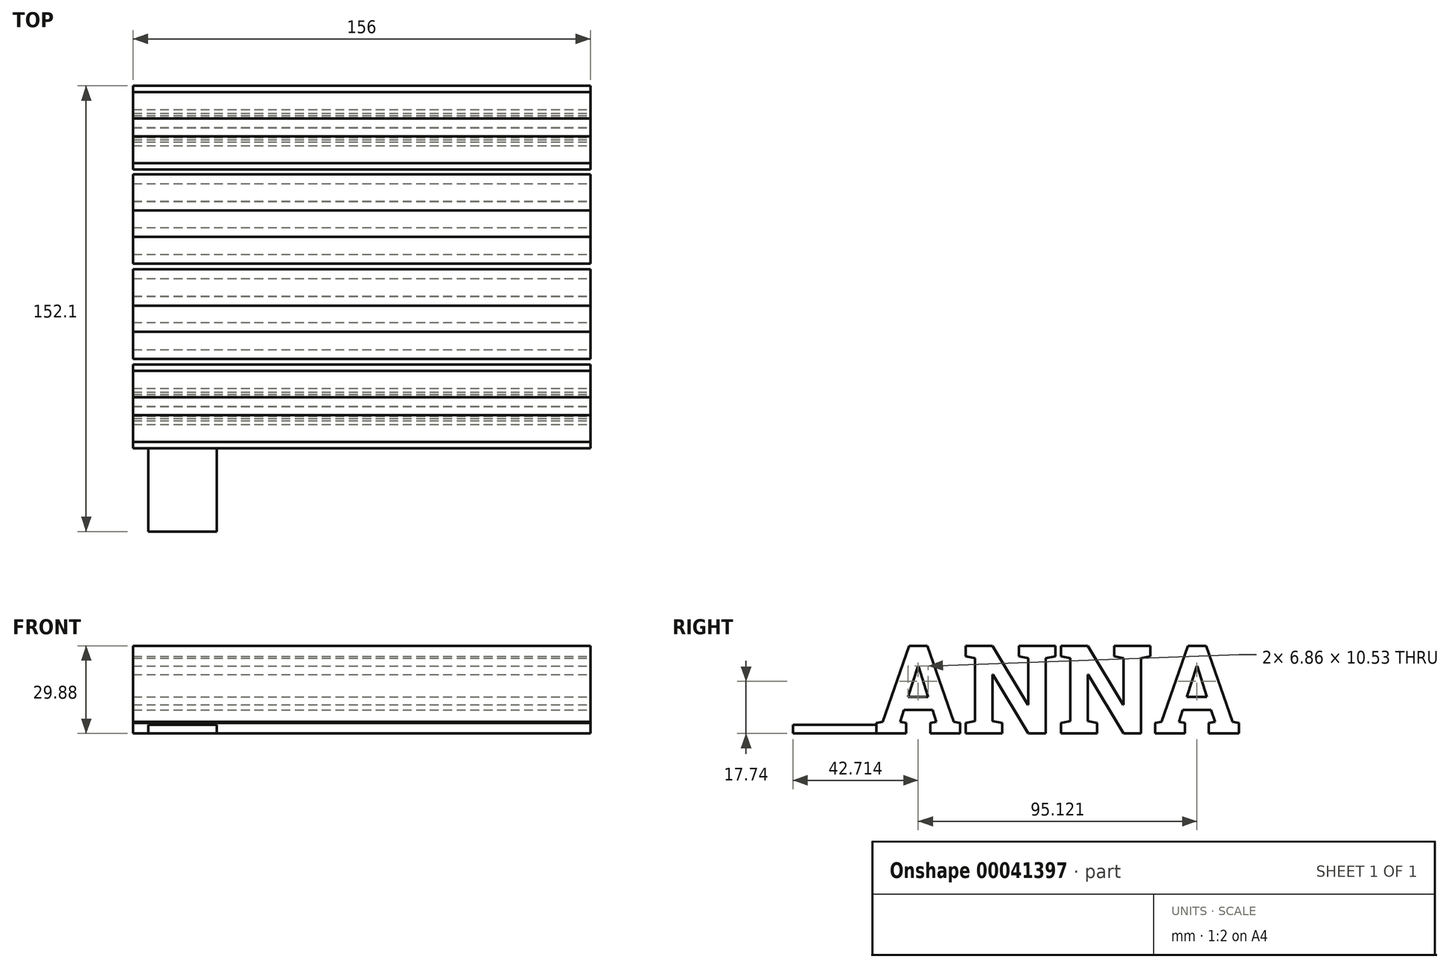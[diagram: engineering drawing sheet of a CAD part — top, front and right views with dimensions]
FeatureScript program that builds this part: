
annotation { "Feature Type Name" : "Feature", "Feature Type Description" : "" }
export const myFeature = defineFeature(function(context is Context, id is Id, definition is map)
    precondition{}
    {
        {
            var Q0;
            Q0=qCreatedBy(makeId("Top.planeOp"),FACE);
            var sketch = newSketch(context, id + "F0", { "sketchPlane" : qUnion([Q0])});
            skLineSegment(sketch, "E0.rect.bottom", {"start": v(78.5, 67.5) * mm, "end": v(-78.5, 67.5) * mm});
            skLineSegment(sketch, "E0.rect.top", {"start": v(78.5, -67.5) * mm, "end": v(-78.5, -67.5) * mm});
            skLineSegment(sketch, "E0.rect.left", {"start": v(78.5, 67.5) * mm, "end": v(78.5, -67.5) * mm});
            skLineSegment(sketch, "E0.rect.right", {"start": v(-78.5, 67.5) * mm, "end": v(-78.5, -67.5) * mm});
            skPoint(sketch, "E0.rect.middle", {"position": v(0, 0) * mm});
            skSolve(sketch);
        }
        {
            var Q0;
            Q0=makeQuery(id+"F0.imprint","IMPRINT",FACE,{"disambiguationData":[TD([[makeQuery(id+"F0.imprint","IMPRINT",EDGE,{"derivedFrom":sQuery(id+"F0.wireOp",EDGE,"E0.rect.bottom")}),1.0]])]});
            extrude(context, id + "F1", {"entities" : qUnion([Q0]), "depth" : 3 * mm});
        }
        {
            var Q0;
            Q0=qSketchRegion(id+"F0",true);
            extrude(context, id + "F2", {"entities" : qUnion([Q0]), "depth" : 3 * mm});
        }
        {
            var Q0;
            Q0=makeQuery(id+"F2.opExtrude","SWEPT_FACE",FACE,{"disambiguationData":[OSD([sQuery(id+"F0.wireOp",EDGE,"E0.rect.top")])]});
            var sketch = newSketch(context, id + "F3", { "sketchPlane" : qUnion([Q0])});
            skText(sketch, "E1", { "text": "EMBLA", "fontName": "RobotoSlab-Bold.ttf"});
            const initialGuessF3  = {"E1": [-0.0735, 0, 1, 0, 0.03]};
            skSetInitialGuess(sketch, initialGuessF3);
            skSolve(sketch);
        }
        {
            var Q0;
            Q0=makeQuery(id+"F1.opExtrude","SWEPT_FACE",FACE,{"disambiguationData":[OSD([sQuery(id+"F0.wireOp",EDGE,"E0.rect.left")])]});
            var sketch = newSketch(context, id + "F4", { "sketchPlane" : qUnion([Q0])});
            skText(sketch, "E2", { "text": "ANNA", "fontName": "RobotoSlab-Bold.ttf"});
            const initialGuessF4  = {"E2": [-0.03405, 0, 1, 0, 0.03026]};
            skSetInitialGuess(sketch, initialGuessF4);
            skSolve(sketch);
        }
        {
            var Q0;
            Q0=qSketchRegion(id+"F3",true);
            extrude(context, id + "F5", {"entities" : qUnion([Q0]), "oppositeDirection" : true, "depth" : 135 * mm});
        }
        {
            var Q0;
            Q0=qSketchRegion(id+"F4",true);
            extrude(context, id + "F6", {"entities" : qUnion([Q0]), "oppositeDirection" : true, "depth" : 156 * mm});
        }
        {
            var Q0;
            Q0=makeQuery(id+"F2.opExtrude","SWEPT_BODY",BODY,{"disambiguationData":[OSD([sQuery(id+"F0.wireOp",EDGE,"E0.rect.bottom"),sQuery(id+"F0.wireOp",EDGE,"E0.rect.top"),sQuery(id+"F0.wireOp",EDGE,"E0.rect.left"),sQuery(id+"F0.wireOp",EDGE,"E0.rect.right")])]});
            var Q1;
            Q1=makeQuery(id+"F5.opExtrude","SWEPT_BODY",BODY,{"disambiguationData":[OSD([sQuery(id+"F3.wireOp",EDGE,"E1.sketch_text.stroke-0"),sQuery(id+"F3.wireOp",EDGE,"E1.sketch_text.stroke-1"),sQuery(id+"F3.wireOp",EDGE,"E1.sketch_text.stroke-2"),sQuery(id+"F3.wireOp",EDGE,"E1.sketch_text.stroke-3"),sQuery(id+"F3.wireOp",EDGE,"E1.sketch_text.stroke-4"),sQuery(id+"F3.wireOp",EDGE,"E1.sketch_text.stroke-5"),sQuery(id+"F3.wireOp",EDGE,"E1.sketch_text.stroke-6"),sQuery(id+"F3.wireOp",EDGE,"E1.sketch_text.stroke-7"),sQuery(id+"F3.wireOp",EDGE,"E1.sketch_text.stroke-8"),sQuery(id+"F3.wireOp",EDGE,"E1.sketch_text.stroke-9"),sQuery(id+"F3.wireOp",EDGE,"E1.sketch_text.stroke-10"),sQuery(id+"F3.wireOp",EDGE,"E1.sketch_text.stroke-11"),sQuery(id+"F3.wireOp",EDGE,"E1.sketch_text.stroke-12"),sQuery(id+"F3.wireOp",EDGE,"E1.sketch_text.stroke-13"),sQuery(id+"F3.wireOp",EDGE,"E1.sketch_text.stroke-14"),sQuery(id+"F3.wireOp",EDGE,"E1.sketch_text.stroke-15"),sQuery(id+"F3.wireOp",EDGE,"E1.sketch_text.stroke-16"),sQuery(id+"F3.wireOp",EDGE,"E1.sketch_text.stroke-17"),sQuery(id+"F3.wireOp",EDGE,"E1.sketch_text.stroke-18"),sQuery(id+"F3.wireOp",EDGE,"E1.sketch_text.stroke-19"),sQuery(id+"F3.wireOp",EDGE,"E1.sketch_text.stroke-20")])]});
            var Q2;
            Q2=makeQuery(id+"F5.opExtrude","SWEPT_BODY",BODY,{"disambiguationData":[OSD([sQuery(id+"F3.wireOp",EDGE,"E1.sketch_text.stroke-21"),sQuery(id+"F3.wireOp",EDGE,"E1.sketch_text.stroke-22"),sQuery(id+"F3.wireOp",EDGE,"E1.sketch_text.stroke-23"),sQuery(id+"F3.wireOp",EDGE,"E1.sketch_text.stroke-24"),sQuery(id+"F3.wireOp",EDGE,"E1.sketch_text.stroke-25"),sQuery(id+"F3.wireOp",EDGE,"E1.sketch_text.stroke-26"),sQuery(id+"F3.wireOp",EDGE,"E1.sketch_text.stroke-27"),sQuery(id+"F3.wireOp",EDGE,"E1.sketch_text.stroke-28"),sQuery(id+"F3.wireOp",EDGE,"E1.sketch_text.stroke-29"),sQuery(id+"F3.wireOp",EDGE,"E1.sketch_text.stroke-30"),sQuery(id+"F3.wireOp",EDGE,"E1.sketch_text.stroke-31"),sQuery(id+"F3.wireOp",EDGE,"E1.sketch_text.stroke-32"),sQuery(id+"F3.wireOp",EDGE,"E1.sketch_text.stroke-33"),sQuery(id+"F3.wireOp",EDGE,"E1.sketch_text.stroke-34"),sQuery(id+"F3.wireOp",EDGE,"E1.sketch_text.stroke-35"),sQuery(id+"F3.wireOp",EDGE,"E1.sketch_text.stroke-36"),sQuery(id+"F3.wireOp",EDGE,"E1.sketch_text.stroke-37"),sQuery(id+"F3.wireOp",EDGE,"E1.sketch_text.stroke-38"),sQuery(id+"F3.wireOp",EDGE,"E1.sketch_text.stroke-39"),sQuery(id+"F3.wireOp",EDGE,"E1.sketch_text.stroke-40"),sQuery(id+"F3.wireOp",EDGE,"E1.sketch_text.stroke-41"),sQuery(id+"F3.wireOp",EDGE,"E1.sketch_text.stroke-42"),sQuery(id+"F3.wireOp",EDGE,"E1.sketch_text.stroke-43"),sQuery(id+"F3.wireOp",EDGE,"E1.sketch_text.stroke-44"),sQuery(id+"F3.wireOp",EDGE,"E1.sketch_text.stroke-45"),sQuery(id+"F3.wireOp",EDGE,"E1.sketch_text.stroke-46"),sQuery(id+"F3.wireOp",EDGE,"E1.sketch_text.stroke-47"),sQuery(id+"F3.wireOp",EDGE,"E1.sketch_text.stroke-48"),sQuery(id+"F3.wireOp",EDGE,"E1.sketch_text.stroke-49"),sQuery(id+"F3.wireOp",EDGE,"E1.sketch_text.stroke-50"),sQuery(id+"F3.wireOp",EDGE,"E1.sketch_text.stroke-51")])]});
            var Q3;
            Q3=makeQuery(id+"F5.opExtrude","SWEPT_BODY",BODY,{"disambiguationData":[OSD([sQuery(id+"F3.wireOp",EDGE,"E1.sketch_text.stroke-52"),sQuery(id+"F3.wireOp",EDGE,"E1.sketch_text.stroke-53"),sQuery(id+"F3.wireOp",EDGE,"E1.sketch_text.stroke-54"),sQuery(id+"F3.wireOp",EDGE,"E1.sketch_text.stroke-55"),sQuery(id+"F3.wireOp",EDGE,"E1.sketch_text.stroke-56"),sQuery(id+"F3.wireOp",EDGE,"E1.sketch_text.stroke-57"),sQuery(id+"F3.wireOp",EDGE,"E1.sketch_text.stroke-58"),sQuery(id+"F3.wireOp",EDGE,"E1.sketch_text.stroke-59"),sQuery(id+"F3.wireOp",EDGE,"E1.sketch_text.stroke-60"),sQuery(id+"F3.wireOp",EDGE,"E1.sketch_text.stroke-61"),sQuery(id+"F3.wireOp",EDGE,"E1.sketch_text.stroke-62"),sQuery(id+"F3.wireOp",EDGE,"E1.sketch_text.stroke-63"),sQuery(id+"F3.wireOp",EDGE,"E1.sketch_text.stroke-64"),sQuery(id+"F3.wireOp",EDGE,"E1.sketch_text.stroke-65"),sQuery(id+"F3.wireOp",EDGE,"E1.sketch_text.stroke-66"),sQuery(id+"F3.wireOp",EDGE,"E1.sketch_text.stroke-67"),sQuery(id+"F3.wireOp",EDGE,"E1.sketch_text.stroke-68"),sQuery(id+"F3.wireOp",EDGE,"E1.sketch_text.stroke-69"),sQuery(id+"F3.wireOp",EDGE,"E1.sketch_text.stroke-70"),sQuery(id+"F3.wireOp",EDGE,"E1.sketch_text.stroke-71"),sQuery(id+"F3.wireOp",EDGE,"E1.sketch_text.stroke-72"),sQuery(id+"F3.wireOp",EDGE,"E1.sketch_text.stroke-73"),sQuery(id+"F3.wireOp",EDGE,"E1.sketch_text.stroke-74"),sQuery(id+"F3.wireOp",EDGE,"E1.sketch_text.stroke-75"),sQuery(id+"F3.wireOp",EDGE,"E1.sketch_text.stroke-76"),sQuery(id+"F3.wireOp",EDGE,"E1.sketch_text.stroke-77"),sQuery(id+"F3.wireOp",EDGE,"E1.sketch_text.stroke-78"),sQuery(id+"F3.wireOp",EDGE,"E1.sketch_text.stroke-79"),sQuery(id+"F3.wireOp",EDGE,"E1.sketch_text.stroke-80"),sQuery(id+"F3.wireOp",EDGE,"E1.sketch_text.stroke-81")])]});
            var Q4;
            Q4=makeQuery(id+"F5.opExtrude","SWEPT_BODY",BODY,{"disambiguationData":[OSD([sQuery(id+"F3.wireOp",EDGE,"E1.sketch_text.stroke-82"),sQuery(id+"F3.wireOp",EDGE,"E1.sketch_text.stroke-83"),sQuery(id+"F3.wireOp",EDGE,"E1.sketch_text.stroke-84"),sQuery(id+"F3.wireOp",EDGE,"E1.sketch_text.stroke-85"),sQuery(id+"F3.wireOp",EDGE,"E1.sketch_text.stroke-86"),sQuery(id+"F3.wireOp",EDGE,"E1.sketch_text.stroke-87"),sQuery(id+"F3.wireOp",EDGE,"E1.sketch_text.stroke-88"),sQuery(id+"F3.wireOp",EDGE,"E1.sketch_text.stroke-89"),sQuery(id+"F3.wireOp",EDGE,"E1.sketch_text.stroke-90"),sQuery(id+"F3.wireOp",EDGE,"E1.sketch_text.stroke-91"),sQuery(id+"F3.wireOp",EDGE,"E1.sketch_text.stroke-92"),sQuery(id+"F3.wireOp",EDGE,"E1.sketch_text.stroke-93"),sQuery(id+"F3.wireOp",EDGE,"E1.sketch_text.stroke-94"),sQuery(id+"F3.wireOp",EDGE,"E1.sketch_text.stroke-95"),sQuery(id+"F3.wireOp",EDGE,"E1.sketch_text.stroke-96"),sQuery(id+"F3.wireOp",EDGE,"E1.sketch_text.stroke-97")])]});
            var Q5;
            Q5=makeQuery(id+"F5.opExtrude","SWEPT_BODY",BODY,{"disambiguationData":[OSD([sQuery(id+"F3.wireOp",EDGE,"E1.sketch_text.stroke-98"),sQuery(id+"F3.wireOp",EDGE,"E1.sketch_text.stroke-99"),sQuery(id+"F3.wireOp",EDGE,"E1.sketch_text.stroke-100"),sQuery(id+"F3.wireOp",EDGE,"E1.sketch_text.stroke-101"),sQuery(id+"F3.wireOp",EDGE,"E1.sketch_text.stroke-102"),sQuery(id+"F3.wireOp",EDGE,"E1.sketch_text.stroke-103"),sQuery(id+"F3.wireOp",EDGE,"E1.sketch_text.stroke-104"),sQuery(id+"F3.wireOp",EDGE,"E1.sketch_text.stroke-105"),sQuery(id+"F3.wireOp",EDGE,"E1.sketch_text.stroke-106"),sQuery(id+"F3.wireOp",EDGE,"E1.sketch_text.stroke-107"),sQuery(id+"F3.wireOp",EDGE,"E1.sketch_text.stroke-108"),sQuery(id+"F3.wireOp",EDGE,"E1.sketch_text.stroke-109"),sQuery(id+"F3.wireOp",EDGE,"E1.sketch_text.stroke-110"),sQuery(id+"F3.wireOp",EDGE,"E1.sketch_text.stroke-111"),sQuery(id+"F3.wireOp",EDGE,"E1.sketch_text.stroke-112"),sQuery(id+"F3.wireOp",EDGE,"E1.sketch_text.stroke-113"),sQuery(id+"F3.wireOp",EDGE,"E1.sketch_text.stroke-114"),sQuery(id+"F3.wireOp",EDGE,"E1.sketch_text.stroke-115"),sQuery(id+"F3.wireOp",EDGE,"E1.sketch_text.stroke-116"),sQuery(id+"F3.wireOp",EDGE,"E1.sketch_text.stroke-117")])]});
            booleanBodies(context, id + "F7", {"operationType" : BooleanOperationType.UNION, "tools" : qUnion([Q0, Q1, Q2, Q3, Q4, Q5])});
        }
        {
            var Q0;
            Q0=makeQuery(id+"F1.opExtrude","SWEPT_BODY",BODY,{"disambiguationData":[OSD([sQuery(id+"F0.wireOp",EDGE,"E0.rect.bottom"),sQuery(id+"F0.wireOp",EDGE,"E0.rect.top"),sQuery(id+"F0.wireOp",EDGE,"E0.rect.left"),sQuery(id+"F0.wireOp",EDGE,"E0.rect.right")])]});
            var Q1;
            Q1=makeQuery(id+"F2.opExtrude","SWEPT_BODY",BODY,{"disambiguationData":[OSD([sQuery(id+"F0.wireOp",EDGE,"E0.rect.bottom"),sQuery(id+"F0.wireOp",EDGE,"E0.rect.top"),sQuery(id+"F0.wireOp",EDGE,"E0.rect.left"),sQuery(id+"F0.wireOp",EDGE,"E0.rect.right")])]});
            booleanBodies(context, id + "F8", {"operationType" : BooleanOperationType.INTERSECTION, "tools" : qUnion([Q0, Q1])});
        }
        {
            var Q0;
            {var subQ0=sQuery(id+"F0.wireOp",EDGE,"E0.rect.bottom");var subQ1=sQuery(id+"F0.wireOp",EDGE,"E0.rect.top");var subQ2=sQuery(id+"F0.wireOp",EDGE,"E0.rect.left");var subQ3=sQuery(id+"F0.wireOp",EDGE,"E0.rect.right");var subQ4=makeQuery(id+"F2.opExtrude","CAP_FACE",FACE,{"disambiguationData":[OSD([subQ0,subQ1,subQ2,subQ3])],"isStart":false});var subQ19=sQuery(id+"F3.wireOp",EDGE,"E1.sketch_text.stroke-96");var subQ29=sQuery(id+"F3.wireOp",EDGE,"E1.sketch_text.stroke-105");var subQ48=sQuery(id+"F3.wireOp",EDGE,"E1.sketch_text.stroke-5");var subQ67=sQuery(id+"F3.wireOp",EDGE,"E1.sketch_text.stroke-22");var subQ69=sQuery(id+"F3.wireOp",EDGE,"E1.sketch_text.stroke-24");var subQ91=sQuery(id+"F3.wireOp",EDGE,"E1.sketch_text.stroke-46");var subQ105=sQuery(id+"F3.wireOp",EDGE,"E1.sketch_text.stroke-58");Q0=makeQuery(id+"F8.opBoolean","MERGE",FACE,{"derivedFrom":[makeQuery(id+"F7.opBoolean","SPLIT",FACE,{"disambiguationData":[TD([makeQuery(id+"F2.opExtrude","SWEPT_FACE",FACE,{"disambiguationData":[OSD([subQ2])]})])],"derivedFrom":subQ4}),makeQuery(id+"F7.opBoolean","SPLIT",FACE,{"disambiguationData":[TD([makeQuery(id+"F2.opExtrude","SWEPT_FACE",FACE,{"disambiguationData":[OSD([subQ3])]})])],"derivedFrom":subQ4}),makeQuery(id+"F7.opBoolean","SPLIT",FACE,{"disambiguationData":[TD([makeQuery(id+"F5.opExtrude","SWEPT_FACE",FACE,{"disambiguationData":[OSD([subQ48])]})])],"derivedFrom":subQ4}),makeQuery(id+"F7.opBoolean","SPLIT",FACE,{"disambiguationData":[TD([makeQuery(id+"F5.opExtrude","SWEPT_FACE",FACE,{"disambiguationData":[OSD([subQ67])]})])],"derivedFrom":subQ4}),makeQuery(id+"F7.opBoolean","SPLIT",FACE,{"disambiguationData":[TD([makeQuery(id+"F5.opExtrude","SWEPT_FACE",FACE,{"disambiguationData":[OSD([subQ69])]})])],"derivedFrom":subQ4}),makeQuery(id+"F7.opBoolean","SPLIT",FACE,{"disambiguationData":[TD([makeQuery(id+"F5.opExtrude","SWEPT_FACE",FACE,{"disambiguationData":[OSD([subQ91])]})])],"derivedFrom":subQ4}),makeQuery(id+"F7.opBoolean","SPLIT",FACE,{"disambiguationData":[TD([makeQuery(id+"F5.opExtrude","SWEPT_FACE",FACE,{"disambiguationData":[OSD([subQ105])]})])],"derivedFrom":subQ4}),makeQuery(id+"F7.opBoolean","SPLIT",FACE,{"disambiguationData":[TD([makeQuery(id+"F5.opExtrude","SWEPT_FACE",FACE,{"disambiguationData":[OSD([subQ19])]})])],"derivedFrom":subQ4}),makeQuery(id+"F7.opBoolean","SPLIT",FACE,{"disambiguationData":[TD([makeQuery(id+"F5.opExtrude","SWEPT_FACE",FACE,{"disambiguationData":[OSD([subQ29])]})])],"derivedFrom":subQ4}),makeQuery(id+"F1.opExtrude","CAP_FACE",FACE,{"disambiguationData":[OSD([subQ0,subQ1,subQ2,subQ3])],"isStart":false})]});}
            var sketch = newSketch(context, id + "F9", { "sketchPlane" : qUnion([Q0])});
            skLineSegment(sketch, "E3.bottom", {"start": v(-48.92, -33.13) * mm, "end": v(-72.36, -33.13) * mm});
            skLineSegment(sketch, "E3.top", {"start": v(-48.92, -61.66) * mm, "end": v(-72.36, -61.66) * mm});
            skLineSegment(sketch, "E3.left", {"start": v(-48.92, -33.13) * mm, "end": v(-48.92, -61.66) * mm});
            skLineSegment(sketch, "E3.right", {"start": v(-72.36, -33.13) * mm, "end": v(-72.36, -61.66) * mm});
            skSolve(sketch);
        }
        {
            var Q0;
            Q0 = qSketchRegion(id + "F9", true);
            extrude(context, id + "F10", {"entities" : qUnion([Q0]), "endBound" : BoundingType.SYMMETRIC, "depth" : 80 * mm});
        }
        {
            var Q0;
            {var subQ0=sQuery(id+"F0.wireOp",EDGE,"E0.rect.bottom");var subQ1=sQuery(id+"F0.wireOp",EDGE,"E0.rect.top");var subQ2=sQuery(id+"F0.wireOp",EDGE,"E0.rect.left");var subQ3=sQuery(id+"F0.wireOp",EDGE,"E0.rect.right");Q0=makeQuery(id+"F8.opBoolean","INTERSECT",BODY,{"derivedFrom":[makeQuery(id+"F1.opExtrude","SWEPT_BODY",BODY,{"disambiguationData":[OSD([subQ0,subQ1,subQ2,subQ3])]}),makeQuery(id+"F2.opExtrude","SWEPT_BODY",BODY,{"disambiguationData":[OSD([subQ0,subQ1,subQ2,subQ3])]})]});}
            var Q1;
            Q1=makeQuery(id+"F10.opExtrude","SWEPT_BODY",BODY,{"disambiguationData":[OSD([sQuery(id+"F9.wireOp",EDGE,"E3.bottom"),sQuery(id+"F9.wireOp",EDGE,"E3.top"),sQuery(id+"F9.wireOp",EDGE,"E3.left"),sQuery(id+"F9.wireOp",EDGE,"E3.right")])]});
            booleanBodies(context, id + "F11", {"operationType" : BooleanOperationType.INTERSECTION, "tools" : qUnion([Q0, Q1])});
        }
    });
